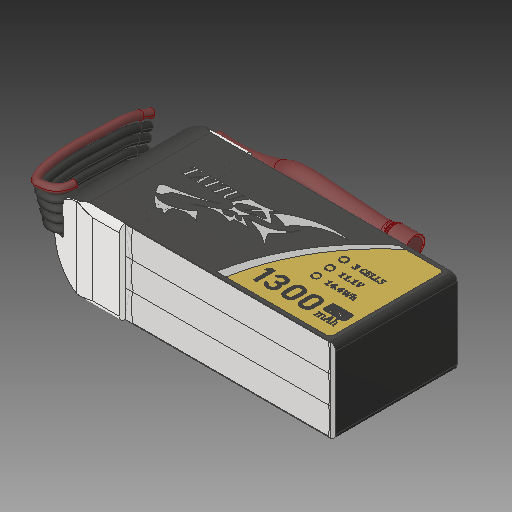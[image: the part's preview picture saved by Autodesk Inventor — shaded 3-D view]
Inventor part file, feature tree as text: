
AUTODESK INVENTOR PART (.ipt)
format: ipt  version: 2019 (Build 230136000, 136)  size: 1,779,712 bytes
history: mixed  units: mm
features: other x18, mirror x2, revolve x2, imported_body x1
ambient origin geometry x8: Origin, YZ Plane, XZ Plane, XY Plane, X Axis, Y Axis, Z Axis, Center Point
bodies: Body1 (imported_parasolid), Body2 (imported_parasolid), Body3 (imported_parasolid), Body4 (imported_parasolid), Body5 (imported_parasolid), Body6 (imported_parasolid), Body7 (imported_parasolid), Body8 (imported_parasolid), Body9 (imported_parasolid), Body10 (imported_parasolid), Body11 (imported_parasolid)
feature tree (23):
  other  "Твердое тело1"
  other  "Твердое тело2"
  other  "Твердое тело3"
  other  "Твердое тело4"
  other  "Твердое тело5"
  other  "Твердое тело6"
  other  "Твердое тело7"
  other  "Твердое тело8"
  other  "Твердое тело9"
  other  "Твердое тело10"
  other  "Твердое тело11"
  other  "Saliente-Extruir2"
  mirror  "Simetría2"
  mirror  "Simetría3"
  other  "Cortar-Extruir8"
  other  "Barrer5[1]"
  other  "Barrer5[2]"
  other  "Barrer5[3]"
  other  "Barrer5[4]"
  other  "Barrer5[5]"
  revolve  "Revolución3"  [1 undecoded]
  revolve  "Revolución4"  [1 undecoded]
  imported_body  NMx_Import_Brep_tag  [imported B-rep: ~21 faces, bbox_mm=None]
note: 2 required parameter values undecoded (feature->parameter linkage not recoverable at this tier; creation-order binding heuristic only, values carry confidence <= 0.55)
